# Revit family: Podajnik_do_recznikow_ZZ DUO S
name_source: partatom
category: Furniture
units: mm (PartAtom-declared; Revit-internal decimal feet)

## family parameters
Always vertical = Yes
Cut with Voids When Loaded = No
Host = Wall
Room Calculation Point = No
Shared = No

## types (1)
- Type 1
    Depth / Glebokosc = 120 mm  [stored 0.393701 ft]
    Description = Podajnik ZZ DUO S to solidny i trwały dozownik jednorazowych, uniwersalnych ręczników papierowych. Do jego produkcji użyto odporną na uszkodzenia stal nierdzewną. Polerowane wykończenie nadaje mu elegancji i sprawia, że pojemnik na ręczniki DUO dodaje uroku każdemu wnętrzu. Idealnie pasuje do obiektów użyteczności publicznej o niskim i średnim natężeniu ruchu, z powodzeniem zastępując suszarki do rąk. Dzięki wbudowanemu okienku w kształcie litery „S” umożliwia kontrolę ilości wkładu w środku, gwarantując tym samym sprawne uzupełnianie ręczników.
    Height / Wysokosc = 210 mm
    Manufacturer = FANECO.com
    Manufacturer code / Kod producenta = 5901764292548
    Material = Stal nierdzewna polerowana
    Material finish / Wykonczenie = Stal nierdzewna 430 polerowana
    Model = HIT S
    Product code / Kod produktu = P300SJP
    URL = https://faneco.com
    Weight / Waga = 1.5 kg
    Width / Szerokosc = 270 mm

note: [stored X ft] marks values corroborated as IEEE doubles in the binary element streams (Revit-internal decimal feet)

## geometry (parser evidence)
native form markers: Blend x16, Sweep x16
no freeform markers — native parametric forms only
